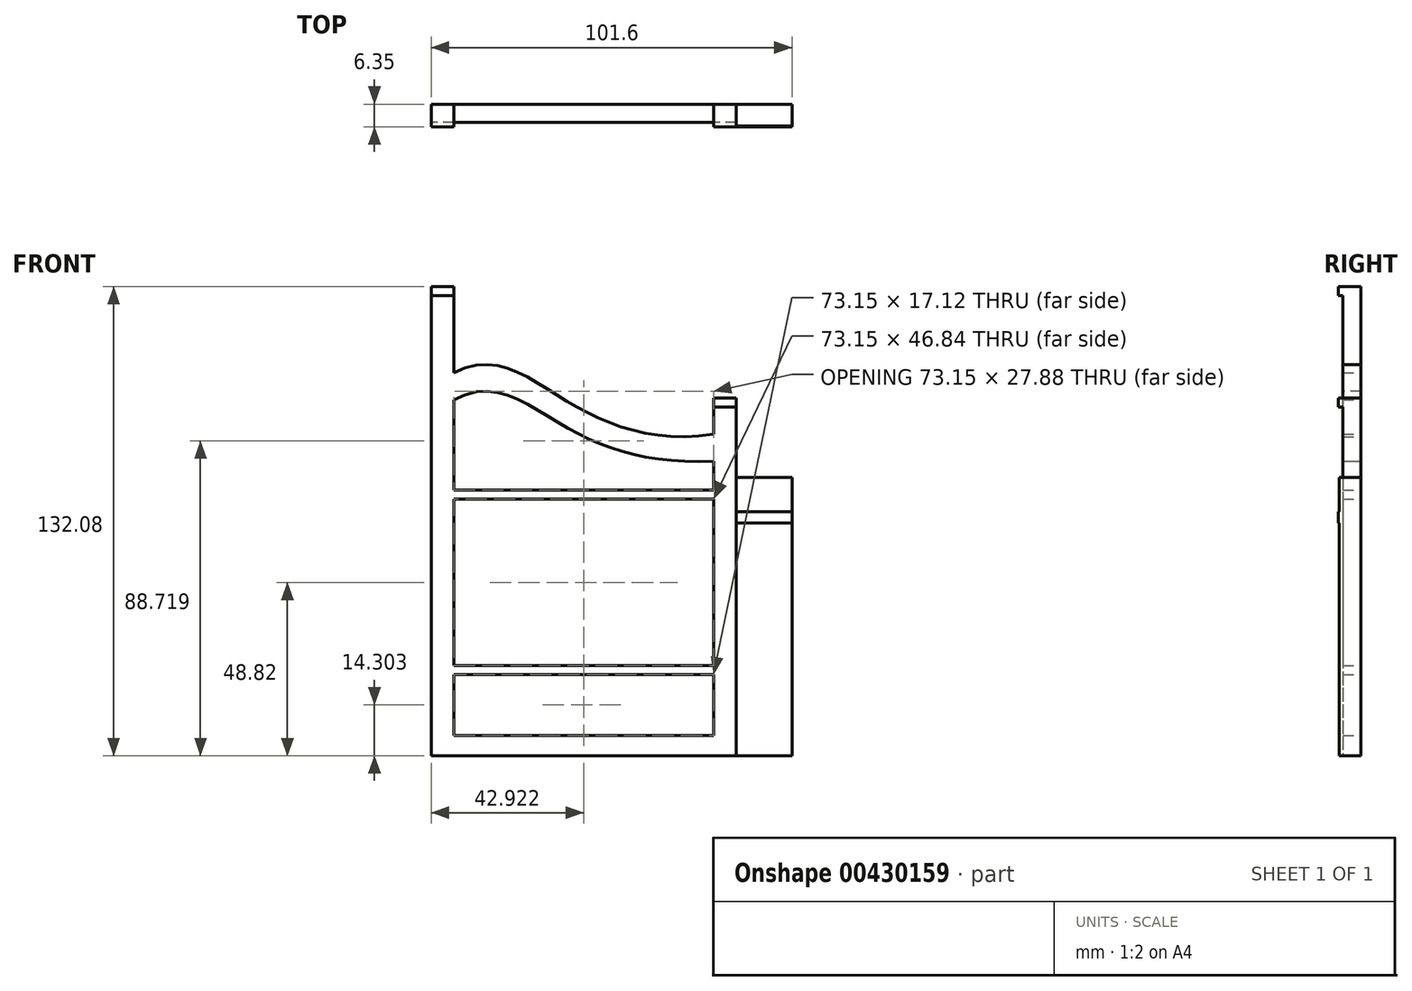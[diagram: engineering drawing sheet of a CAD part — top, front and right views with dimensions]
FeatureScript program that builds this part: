
annotation { "Feature Type Name" : "Feature", "Feature Type Description" : "" }
export const myFeature = defineFeature(function(context is Context, id is Id, definition is map)
    precondition{}
    {
        {
            var Q0;
            Q0=qCreatedBy(makeId("Front.planeOp"),FACE);
            var sketch = newSketch(context, id + "F0", { "sketchPlane" : qUnion([Q0])});
            skLineSegment(sketch, "E0.bottom", {"start": v(-8.04, -6.74) * mm, "end": v(-8.04, -6.74) * mm});
            skLineSegment(sketch, "E0.top", {"start": v(-8.04, -1) * mm, "end": v(-8.04, -1) * mm});
            skLineSegment(sketch, "E1.MirrorCS", {"start": v(28.9, -57.38) * mm, "end": v(28.9, -63.13) * mm});
            skLineSegment(sketch, "E2.MirrorCS", {"start": v(28.9, -63.13) * mm, "end": v(28.9, -57.38) * mm});
            skLineSegment(sketch, "E3.MirrorCS", {"start": v(35.26, 35.04) * mm, "end": v(28.9, 35.04) * mm});
            skLineSegment(sketch, "E4.MirrorCS", {"start": v(35.26, -63.13) * mm, "end": v(28.9, -63.13) * mm});
            skLineSegment(sketch, "E5.MirrorCS", {"start": v(35.26, 37.58) * mm, "end": v(28.9, 37.58) * mm});
            skLineSegment(sketch, "E6.MirrorCS", {"start": v(28.9, 35.04) * mm, "end": v(28.9, 37.58) * mm});
            skLineSegment(sketch, "E7.MirrorCS", {"start": v(35.26, 37.58) * mm, "end": v(35.26, 35.04) * mm});
            skLineSegment(sketch, "E8.MirrorCS", {"start": v(-44.24, 66.41) * mm, "end": v(-50.6, 66.41) * mm});
            skLineSegment(sketch, "E9.MirrorCS", {"start": v(-44.24, 68.95) * mm, "end": v(-50.6, 68.95) * mm});
            skLineSegment(sketch, "E10.MirrorCS", {"start": v(-50.6, 66.41) * mm, "end": v(-50.6, 68.95) * mm});
            skLineSegment(sketch, "E11.MirrorCS", {"start": v(-44.24, 68.95) * mm, "end": v(-44.24, 66.41) * mm});
            skLineSegment(sketch, "E12.MirrorCS", {"start": v(-44.24, -57.38) * mm, "end": v(-44.24, -63.13) * mm});
            skLineSegment(sketch, "E13.MirrorCS", {"start": v(51, 5.55) * mm, "end": v(51, 2.4) * mm});
            skLineSegment(sketch, "E14.MirrorCS", {"start": v(-44.24, -63.13) * mm, "end": v(-50.6, -63.13) * mm});
            skLineSegment(sketch, "E15.MirrorCS", {"start": v(35.26, 2.4) * mm, "end": v(35.26, 5.55) * mm});
            skLineSegment(sketch, "E16.MirrorCS", {"start": v(28.9, -19.82) * mm, "end": v(-44.24, -19.82) * mm});
            skLineSegment(sketch, "E17.MirrorCS", {"start": v(28.9, 27.46) * mm, "end": v(28.9, 12.22) * mm});
            skLineSegment(sketch, "E18.MirrorCS", {"start": v(28.9, -30.93) * mm, "end": v(-44.24, -30.93) * mm});
            skLineSegment(sketch, "E19.MirrorCS", {"start": v(35.26, 15.18) * mm, "end": v(35.26, -63.13) * mm});
            skLineSegment(sketch, "E20.MirrorCS", {"start": v(-44.24, 44.67) * mm, "end": v(-44.24, 15.18) * mm});
            skLineSegment(sketch, "E21.MirrorCS", {"start": v(51, 2.4) * mm, "end": v(35.26, 2.4) * mm});
            skPoint(sketch, "E22.MirrorP", {"position": v(-50.6, -18.86) * mm});
            skLineSegment(sketch, "E23.MirrorCS", {"start": v(28.9, 9.1) * mm, "end": v(-44.24, 9.1) * mm});
            skLineSegment(sketch, "E24.MirrorCS", {"start": v(-50.6, 68.95) * mm, "end": v(-50.6, -63.13) * mm});
            skLineSegment(sketch, "E25.MirrorCS", {"start": v(28.9, 37.58) * mm, "end": v(28.9, -63.13) * mm});
            skLineSegment(sketch, "E26.MirrorCS", {"start": v(-44.24, 68.95) * mm, "end": v(-44.24, -63.13) * mm});
            skLineSegment(sketch, "E27.MirrorCS", {"start": v(35.26, 37.58) * mm, "end": v(35.26, -63.13) * mm});
            skLineSegment(sketch, "E28.MirrorCS", {"start": v(51, 15.18) * mm, "end": v(51, -63.13) * mm});
            skLineSegment(sketch, "E29.MirrorCS", {"start": v(51, -63.13) * mm, "end": v(35.26, -63.13) * mm});
            skLineSegment(sketch, "E30.MirrorCS", {"start": v(51, 15.18) * mm, "end": v(35.26, 15.18) * mm});
            skFitSpline(sketch, "E31.MirrorCS", {"points": [v(28.9, 19.84) * mm, v(-13.05, 29.64) * mm, v(-44.24, 37.05) * mm], "startDerivative": vector(-97, -4.8) * mm, "endDerivative": vector(-75.65, -43.06) * mm});
            skFitSpline(sketch, "E32.MirrorCS", {"points": [v(28.9, 27.46) * mm, v(-13.84, 37.58) * mm, v(-44.24, 44.67) * mm], "startDerivative": vector(-96.97, -15.79) * mm, "endDerivative": vector(-77.2, -40.21) * mm});
            skLineSegment(sketch, "E33.MirrorCS", {"start": v(35.26, 5.55) * mm, "end": v(51, 5.55) * mm});
            skLineSegment(sketch, "E34.MirrorCS", {"start": v(28.9, -31.88) * mm, "end": v(-44.24, -31.88) * mm});
            skPoint(sketch, "E35.MirrorP", {"position": v(-50.6, -20.77) * mm});
            skLineSegment(sketch, "E36.MirrorCS", {"start": v(28.9, -37.73) * mm, "end": v(-44.24, -37.73) * mm});
            skLineSegment(sketch, "E37.MirrorCS", {"start": v(28.9, -32.83) * mm, "end": v(-44.24, -32.83) * mm});
            skLineSegment(sketch, "E38.MirrorCS", {"start": v(28.9, -63.13) * mm, "end": v(-44.24, -63.13) * mm});
            skPoint(sketch, "E39.MirrorP", {"position": v(-50.6, -32.83) * mm});
            skLineSegment(sketch, "E40.MirrorCS", {"start": v(28.9, 11.65) * mm, "end": v(-44.24, 11.65) * mm});
            skLineSegment(sketch, "E41.MirrorCS", {"start": v(28.9, -57.38) * mm, "end": v(-44.24, -57.38) * mm});
            skLineSegment(sketch, "E42.MirrorCS", {"start": v(28.9, -40.27) * mm, "end": v(-44.24, -40.27) * mm});
            skLineSegment(sketch, "E43.MirrorCS", {"start": v(28.9, -20.77) * mm, "end": v(-44.24, -20.77) * mm});
            skPoint(sketch, "E44.MirrorP", {"position": v(-50.6, -30.93) * mm});
            skLineSegment(sketch, "E45.MirrorCS", {"start": v(28.9, -18.86) * mm, "end": v(-44.24, -18.86) * mm});
            skSolve(sketch);
        }
        {
            var Q0;
            {var subQ8=sQuery(id+"F0.wireOp",EDGE,"a7e12be4-4bf7-41b4-b51e-abff9a2e7cac12.MirrorCS");Q0=makeQuery(id+"F0.imprint","IMPRINT",FACE,{"disambiguationData":[TD([[makeQuery(id+"F0.imprint","IMPRINT",EDGE,{"derivedFrom":subQ8}),1.0]])]});}
            var Q1;
            {var subQ0=sQuery(id+"F0.wireOp",EDGE,"a7e12be4-4bf7-41b4-b51e-abff9a2e7cac40.MirrorCS");Q1=makeQuery(id+"F0.imprint","IMPRINT",FACE,{"disambiguationData":[TD([[makeQuery(id+"F0.imprint","IMPRINT",EDGE,{"derivedFrom":subQ0}),-1.0]])]});}
            var Q2;
            {var subQ8=sQuery(id+"F0.wireOp",EDGE,"a7e12be4-4bf7-41b4-b51e-abff9a2e7cac6.MirrorCS");Q2=makeQuery(id+"F0.imprint","IMPRINT",FACE,{"disambiguationData":[TD([[makeQuery(id+"F0.imprint","IMPRINT",EDGE,{"derivedFrom":subQ8}),1.0]])]});}
            var Q3;
            {var subQ0=sQuery(id+"F0.wireOp",EDGE,"a7e12be4-4bf7-41b4-b51e-abff9a2e7cac24.MirrorCS");Q3=makeQuery(id+"F0.imprint","IMPRINT",FACE,{"disambiguationData":[TD([[makeQuery(id+"F0.imprint","IMPRINT",EDGE,{"derivedFrom":subQ0}),1.0]])]});}
            var Q4;
            {var subQ5=sQuery(id+"F0.wireOp",EDGE,"E8.MirrorCS");Q4=makeQuery(id+"F0.imprint","IMPRINT",FACE,{"disambiguationData":[TD([[makeQuery(id+"F0.imprint","IMPRINT",EDGE,{"derivedFrom":subQ5}),1.0]])]});}
            var Q5;
            {var subQ0=sQuery(id+"F0.wireOp",EDGE,"E31.MirrorCS");Q5=makeQuery(id+"F0.imprint","IMPRINT",FACE,{"disambiguationData":[TD([[makeQuery(id+"F0.imprint","IMPRINT",EDGE,{"derivedFrom":subQ0}),-1.0]])]});}
            var Q6;
            {var subQ8=sQuery(id+"F0.wireOp",EDGE,"E3.MirrorCS");Q6=makeQuery(id+"F0.imprint","IMPRINT",FACE,{"disambiguationData":[TD([[makeQuery(id+"F0.imprint","IMPRINT",EDGE,{"derivedFrom":subQ8}),1.0]])]});}
            var Q7;
            {var subQ0=sQuery(id+"F0.wireOp",EDGE,"E38.MirrorCS");Q7=makeQuery(id+"F0.imprint","IMPRINT",FACE,{"disambiguationData":[TD([[makeQuery(id+"F0.imprint","IMPRINT",EDGE,{"derivedFrom":subQ0}),-1.0]])]});}
            var Q8;
            {var subQ0=sQuery(id+"F0.wireOp",EDGE,"E23.MirrorCS");Q8=makeQuery(id+"F0.imprint","IMPRINT",FACE,{"disambiguationData":[TD([[makeQuery(id+"F0.imprint","IMPRINT",EDGE,{"derivedFrom":subQ0}),-1.0]])]});}
            var Q9;
            {var subQ0=sQuery(id+"F0.wireOp",EDGE,"E36.MirrorCS");Q9=makeQuery(id+"F0.imprint","IMPRINT",FACE,{"disambiguationData":[TD([[makeQuery(id+"F0.imprint","IMPRINT",EDGE,{"derivedFrom":subQ0}),1.0]])]});}
            extrude(context, id + "F1", {"entities" : qUnion([Q0, Q1, Q2, Q3, Q4, Q5, Q6, Q7, Q8, Q9]), "depth" : 5.08 * mm, "offsetDistance" : 25.4 * mm});
        }
        {
            var Q0;
            {var subQ0=sQuery(id+"F0.wireOp",EDGE,"a7e12be4-4bf7-41b4-b51e-abff9a2e7cac12.MirrorCS");Q0=makeQuery(id+"F0.imprint","IMPRINT",FACE,{"disambiguationData":[TD([[makeQuery(id+"F0.imprint","IMPRINT",EDGE,{"derivedFrom":subQ0}),-1.0]])]});}
            var Q1;
            {var subQ0=sQuery(id+"F0.wireOp",EDGE,"a7e12be4-4bf7-41b4-b51e-abff9a2e7cac6.MirrorCS");Q1=makeQuery(id+"F0.imprint","IMPRINT",FACE,{"disambiguationData":[TD([[makeQuery(id+"F0.imprint","IMPRINT",EDGE,{"derivedFrom":subQ0}),-1.0]])]});}
            var Q2;
            {var subQ0=sQuery(id+"F0.wireOp",EDGE,"a7e12be4-4bf7-41b4-b51e-abff9a2e7cac29.MirrorCS");Q2=makeQuery(id+"F0.imprint","IMPRINT",FACE,{"disambiguationData":[TD([[makeQuery(id+"F0.imprint","IMPRINT",EDGE,{"derivedFrom":subQ0}),-1.0]])]});}
            var Q3;
            {var subQ0=sQuery(id+"F0.wireOp",EDGE,"E8.MirrorCS");Q3=makeQuery(id+"F0.imprint","IMPRINT",FACE,{"disambiguationData":[TD([[makeQuery(id+"F0.imprint","IMPRINT",EDGE,{"derivedFrom":subQ0}),-1.0]])]});}
            var Q4;
            {var subQ0=sQuery(id+"F0.wireOp",EDGE,"E3.MirrorCS");Q4=makeQuery(id+"F0.imprint","IMPRINT",FACE,{"disambiguationData":[TD([[makeQuery(id+"F0.imprint","IMPRINT",EDGE,{"derivedFrom":subQ0}),-1.0]])]});}
            var Q5;
            {var subQ0=sQuery(id+"F0.wireOp",EDGE,"E21.MirrorCS");Q5=makeQuery(id+"F0.imprint","IMPRINT",FACE,{"disambiguationData":[TD([[makeQuery(id+"F0.imprint","IMPRINT",EDGE,{"derivedFrom":subQ0}),-1.0]])]});}
            extrude(context, id + "F2", {"entities" : qUnion([Q0, Q1, Q2, Q3, Q4, Q5]), "operationType" : NewBodyOperationType.ADD, "depth" : 6.35 * mm, "offsetDistance" : 25.4 * mm});
        }
        {
            var Q0;
            {var subQ0=sQuery(id+"F0.wireOp",EDGE,"a7e12be4-4bf7-41b4-b51e-abff9a2e7cac39.MirrorCS");Q0=makeQuery(id+"F0.imprint","IMPRINT",FACE,{"disambiguationData":[TD([[makeQuery(id+"F0.imprint","IMPRINT",EDGE,{"derivedFrom":subQ0}),1.0]])]});}
            var Q1;
            {var subQ0=sQuery(id+"F0.wireOp",EDGE,"a7e12be4-4bf7-41b4-b51e-abff9a2e7cac29.MirrorCS");Q1=makeQuery(id+"F0.imprint","IMPRINT",FACE,{"disambiguationData":[TD([[makeQuery(id+"F0.imprint","IMPRINT",EDGE,{"derivedFrom":subQ0}),1.0]])]});}
            var Q2;
            {var subQ0=sQuery(id+"F0.wireOp",EDGE,"E21.MirrorCS");Q2=makeQuery(id+"F0.imprint","IMPRINT",FACE,{"disambiguationData":[TD([[makeQuery(id+"F0.imprint","IMPRINT",EDGE,{"derivedFrom":subQ0}),1.0]])]});}
            var Q3;
            {var subQ0=sQuery(id+"F0.wireOp",EDGE,"E30.MirrorCS");Q3=makeQuery(id+"F0.imprint","IMPRINT",FACE,{"disambiguationData":[TD([[makeQuery(id+"F0.imprint","IMPRINT",EDGE,{"derivedFrom":subQ0}),1.0]])]});}
            extrude(context, id + "F3", {"entities" : qUnion([Q0, Q1, Q2, Q3]), "operationType" : NewBodyOperationType.ADD, "depth" : 6.1 * mm, "offsetDistance" : 25.4 * mm});
        }
    });
